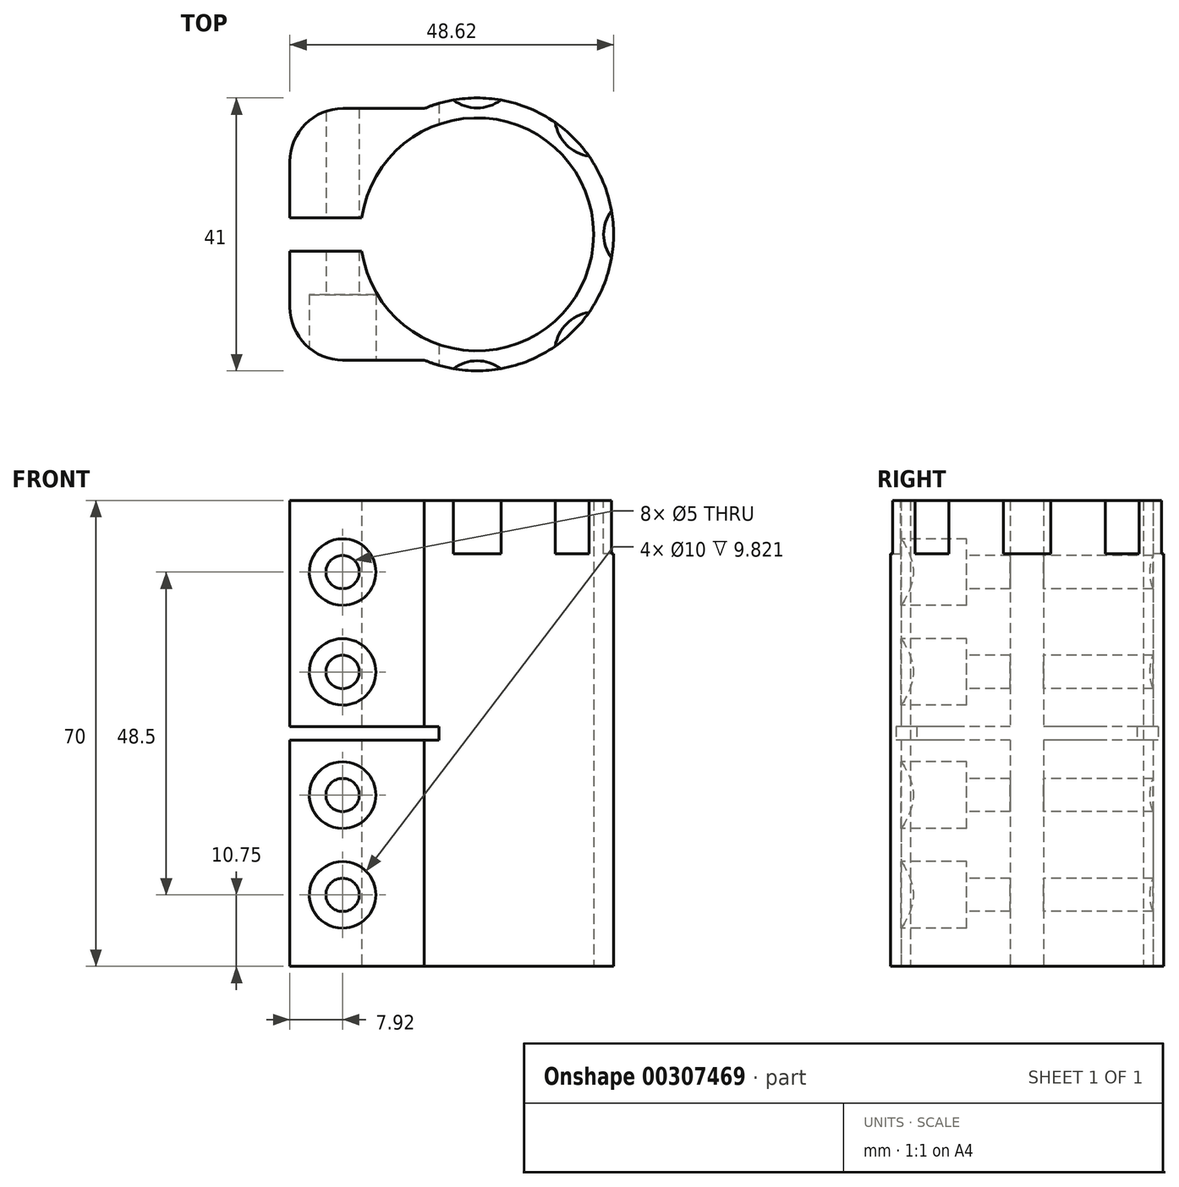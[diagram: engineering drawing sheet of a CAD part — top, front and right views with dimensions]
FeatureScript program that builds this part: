
annotation { "Feature Type Name" : "Feature", "Feature Type Description" : "" }
export const myFeature = defineFeature(function(context is Context, id is Id, definition is map)
    precondition{}
    {
        {
            var Q0;
            Q0=qCreatedBy(makeId("Top.planeOp"),FACE);
            var sketch = newSketch(context, id + "F0", { "sketchPlane" : qUnion([Q0])});
            skArc(sketch, "E0", {"start": v(-17.32, -2.5) * mm, "mid": v(17.5, 0) * mm, "end": v(-17.32, 2.5) * mm});
            skLineSegment(sketch, "E1", {"start": v(-7.92, 18.9) * mm, "end": v(-20.12, 18.9) * mm});
            skLineSegment(sketch, "E2", {"start": v(-28.12, 10.9) * mm, "end": v(-28.12, 2.5) * mm});
            skLineSegment(sketch, "E3", {"start": v(-17.32, 2.5) * mm, "end": v(-28.12, 2.5) * mm});
            skArc(sketch, "E4.filletArc", {"start": v(-20.12, 18.9) * mm, "mid": v(-25.78, 16.57) * mm, "end": v(-28.12, 10.9) * mm});
            skLineSegment(sketch, "E5", {"start": v(0, 0) * mm, "end": v(47.68, 0) * mm});
            skLineSegment(sketch, "E6.MirrorCS", {"start": v(-7.92, -18.9) * mm, "end": v(-20.12, -18.9) * mm});
            skArc(sketch, "E7.MirrorCS", {"start": v(-20.12, -18.9) * mm, "mid": v(-25.78, -16.57) * mm, "end": v(-28.12, -10.9) * mm});
            skLineSegment(sketch, "E8.MirrorCS", {"start": v(-28.12, -10.9) * mm, "end": v(-28.12, -2.5) * mm});
            skLineSegment(sketch, "E9.MirrorCS", {"start": v(-17.32, -2.5) * mm, "end": v(-28.12, -2.5) * mm});
            skArc(sketch, "E10.trimOffspring", {"start": v(-7.92, -18.9) * mm, "mid": v(20.5, 0) * mm, "end": v(-7.92, 18.9) * mm});
            skSolve(sketch);
        }
        {
            var Q0;
            Q0 = qSketchRegion(id + "F0", true);
            extrude(context, id + "F1", {"entities" : qUnion([Q0]), "endBound" : BoundingType.SYMMETRIC, "depth" : 70 * mm, "offsetDistance" : 25 * mm});
        }
        {
            var Q0;
            Q0=makeQuery(id+"F1.opExtrude","SWEPT_FACE",FACE,{"disambiguationData":[OSD([sQuery(id+"F0.wireOp",EDGE,"E6.MirrorCS")])]});
            var sketch = newSketch(context, id + "F2", { "sketchPlane" : qUnion([Q0])});
            skPoint(sketch, "E11", {"position": v(-20.2, -9.25) * mm});
            skPoint(sketch, "E12", {"position": v(-20.2, 9.25) * mm});
            skPoint(sketch, "E13", {"position": v(-20.2, 24.25) * mm});
            skPoint(sketch, "E14", {"position": v(-20.2, -24.25) * mm});
            skSolve(sketch);
        }
        {
            var Q0;
            Q0=sQuery(id+"F2.wireOp",VERTEX,"E13");
            var Q1;
            Q1=sQuery(id+"F2.wireOp",VERTEX,"E12");
            var Q2;
            Q2=sQuery(id+"F2.wireOp",VERTEX,"E11");
            var Q3;
            Q3=sQuery(id+"F2.wireOp",VERTEX,"E14");
            var Q4;
            Q4=makeQuery(id+"F1.opExtrude","SWEPT_BODY",BODY,{"disambiguationData":[OSD([sQuery(id+"F0.wireOp",EDGE,"E0"),sQuery(id+"F0.wireOp",EDGE,"E1"),sQuery(id+"F0.wireOp",EDGE,"E2"),sQuery(id+"F0.wireOp",EDGE,"E3"),sQuery(id+"F0.wireOp",EDGE,"E4.filletArc"),sQuery(id+"F0.wireOp",EDGE,"E6.MirrorCS"),sQuery(id+"F0.wireOp",EDGE,"E7.MirrorCS"),sQuery(id+"F0.wireOp",EDGE,"E8.MirrorCS"),sQuery(id+"F0.wireOp",EDGE,"E9.MirrorCS"),sQuery(id+"F0.wireOp",EDGE,"E10.trimOffspring")])]});
            hole(context, id + "F3", {"style" : HoleStyle.C_BORE, "endStyle" : HoleEndStyle.THROUGH, "holeDiameter" : 5 * mm, "cBoreDiameter" : 10 * mm, "cBoreDepth" : 8 * mm, "majorDiameter" : 5 * mm, "isTappedThrough" : true, "tappedDepth" : 12 * mm, "tapClearance" : 3, "locations" : qUnion([Q0, Q1, Q2, Q3]), "scope" : qUnion([Q4])});
        }
        {
            var Q0;
            Q0=qCreatedBy(makeId("Front.planeOp"),FACE);
            var sketch = newSketch(context, id + "F4", { "sketchPlane" : qUnion([Q0])});
            skLineSegment(sketch, "E15.bottom", {"start": v(-5.72, 1) * mm, "end": v(-28.12, 1) * mm});
            skLineSegment(sketch, "E15.top", {"start": v(-5.72, -1) * mm, "end": v(-28.12, -1) * mm});
            skLineSegment(sketch, "E15.left", {"start": v(-5.72, 1) * mm, "end": v(-5.72, -1) * mm});
            skLineSegment(sketch, "E15.right", {"start": v(-28.12, 1) * mm, "end": v(-28.12, -1) * mm});
            skSolve(sketch);
        }
        {
            var Q0;
            Q0 = qSketchRegion(id + "F4", true);
            extrude(context, id + "F5", {"entities" : qUnion([Q0]), "operationType" : NewBodyOperationType.REMOVE, "endBound" : BoundingType.SYMMETRIC, "oppositeDirection" : true, "depth" : 50 * mm, "offsetDistance" : 25 * mm});
        }
        {
            var Q0;
            Q0=makeQuery(id+"F1.opExtrude","CAP_FACE",FACE,{"disambiguationData":[OSD([sQuery(id+"F0.wireOp",EDGE,"E0"),sQuery(id+"F0.wireOp",EDGE,"E1"),sQuery(id+"F0.wireOp",EDGE,"E2"),sQuery(id+"F0.wireOp",EDGE,"E3"),sQuery(id+"F0.wireOp",EDGE,"E4.filletArc"),sQuery(id+"F0.wireOp",EDGE,"E6.MirrorCS"),sQuery(id+"F0.wireOp",EDGE,"E7.MirrorCS"),sQuery(id+"F0.wireOp",EDGE,"E8.MirrorCS"),sQuery(id+"F0.wireOp",EDGE,"E9.MirrorCS"),sQuery(id+"F0.wireOp",EDGE,"E10.trimOffspring")])],"isStart":false});
            var sketch = newSketch(context, id + "F6", { "sketchPlane" : qUnion([Q0])});
            skCircle(sketch, "E16", {"center": v(0, -25) * mm, "radius": 6 * mm});
            skCircle(sketch, "E17.1.0", {"center": v(17.68, -17.68) * mm, "radius": 6 * mm});
            skCircle(sketch, "E17.2.0", {"center": v(25, 0) * mm, "radius": 6 * mm});
            skCircle(sketch, "E17.3.0", {"center": v(17.68, 17.68) * mm, "radius": 6 * mm});
            skCircle(sketch, "E17.4.0", {"center": v(0, 25) * mm, "radius": 6 * mm});
            skPoint(sketch, "E17.center", {"position": v(0, 0) * mm});
            skLineSegment(sketch, "E17.anchor1", {"start": v(0, 0) * mm, "end": v(0, -25) * mm, "construction": true});
            skLineSegment(sketch, "E17.anchor2", {"start": v(0, 0) * mm, "end": v(0, 25) * mm, "construction": true});
            skSolve(sketch);
        }
        {
            var Q0;
            Q0 = qSketchRegion(id + "F6", true);
            extrude(context, id + "F7", {"entities" : qUnion([Q0]), "operationType" : NewBodyOperationType.REMOVE, "oppositeDirection" : true, "depth" : 8 * mm, "offsetDistance" : 25 * mm});
        }
    });
